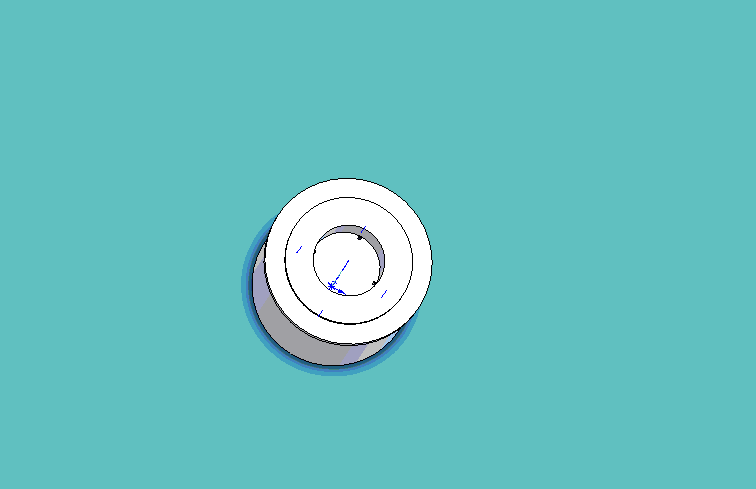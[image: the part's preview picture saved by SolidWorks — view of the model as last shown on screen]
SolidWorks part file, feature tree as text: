
SOLIDWORKS PART (.sldprt)
format: sldprt  version: not decoded by parser v0  size: 109,568 bytes
history: native  units: mm
features: sketch x6, plane x3, extrude x3, cut_extrude x3, pattern_circular x2, material x1 (+10 scaffold rows collapsed)
feature tree (28):
  scaffold x10  (default folders/planes/origin — collapsed)
  material  "Material <not specified>"
  plane  "Frontal"
  plane  "Horizontal"
  plane  "Profile"
  sketch  "Sketch1"  dims[D1=~8.865037mm]
  extrude  "Extrude1"  Depth=17mm
  sketch  "Sketch2"  dims[D1=~11.699626mm]
  extrude  "Extrude3"  Depth=10.5mm
  sketch  "Sketch3"  dims[D1=~10.83074mm]
  extrude  "Extrude4"  Depth=1mm
  sketch  "Sketch4"  dims[D1=9.0mm]
  cut_extrude  "Cut-Extrude1"  Depth=5mm
  sketch  "Sketch6"  dims[D1=~2.123134mm]
  cut_extrude  "Cut-Extrude4"  Depth=5mm
  pattern_circular  "CirPattern1"  Count=4 Angle=360deg
  sketch  "Sketch7"  dims[D1=0.4mm]
  cut_extrude  "Cut-Extrude5"  [1 undecoded]
  pattern_circular  "CirPattern2"  Count=4 Angle=360deg
decode coverage: 13 of 14 modeling features carry decoded parameters
note: ~ marks probable driven/reference dimensions
note: 1 parameter value undecoded
note: suppression state not decoded; provenance and decode notes live in map.json
